# Revit family: Kitchen_Taps-Mixers_hansgrohe_72800JPN-Talis-M54-Single-lever-kitchen_new
name_source: partatom
category: Plumbing Fixtures
revit_build: Autodesk Revit 2018 (Build: 20170223_1515(x64)
units: mm (PartAtom-declared; Revit-internal decimal feet)

## family parameters
Always vertical = No
Cut with Voids When Loaded = No
OmniClass Number = 23.31.11.00
OmniClass Title = Faucets
Part Type = Normal
Room Calculation Point = No
Round Connector Dimension = Use Diameter
Shared = No
Work Plane-Based = Yes

## types (1)
- 004 Chrome
    Always visible = Yes
    BIMobject category = Taps & Mixers
    Connector Description = Water Inlet 9.5mm
    Default Elevation = 1219.2 mm  [stored 4 ft]
    Description = Talis M54 Single lever kitchen mixer 210, pull-out spray, 2jet
    Diameter = 10 mm
    Edition number = 1
    IFC Classification = Valve
    Manufacturer = Hansgrohe
    Manufacturer name = hansgrohe
    Material 1 = Hansgrohe - Metal - 004 Chrome
    Model = 72800JPN
    OmniClass Code = 23-31 11 00
    OmniClass Description = Faucets
    Product Guid = 4d93fe47-7106-43ca-b1a5-f899e94d6896
    Product SKU = 72800JPN
    Product data url = https://bimobject.com
    Product family = Talis M54
    Product group = Kitchen mixers
    Product name = 72800JPN Talis M54 Single lever kitchen mixer 210, pull-out spray, 2jet
    Product url = https://www.hansgrohe.com
    QR code = https://bimobject.com
    URL = https://www.hansgrohe.com
    Weight Net (Kg) = 2.5

note: [stored X ft] marks values corroborated as IEEE doubles in the binary element streams (Revit-internal decimal feet)

## geometry (parser evidence)
native form markers: Sweep x2
no freeform markers — native parametric forms only
